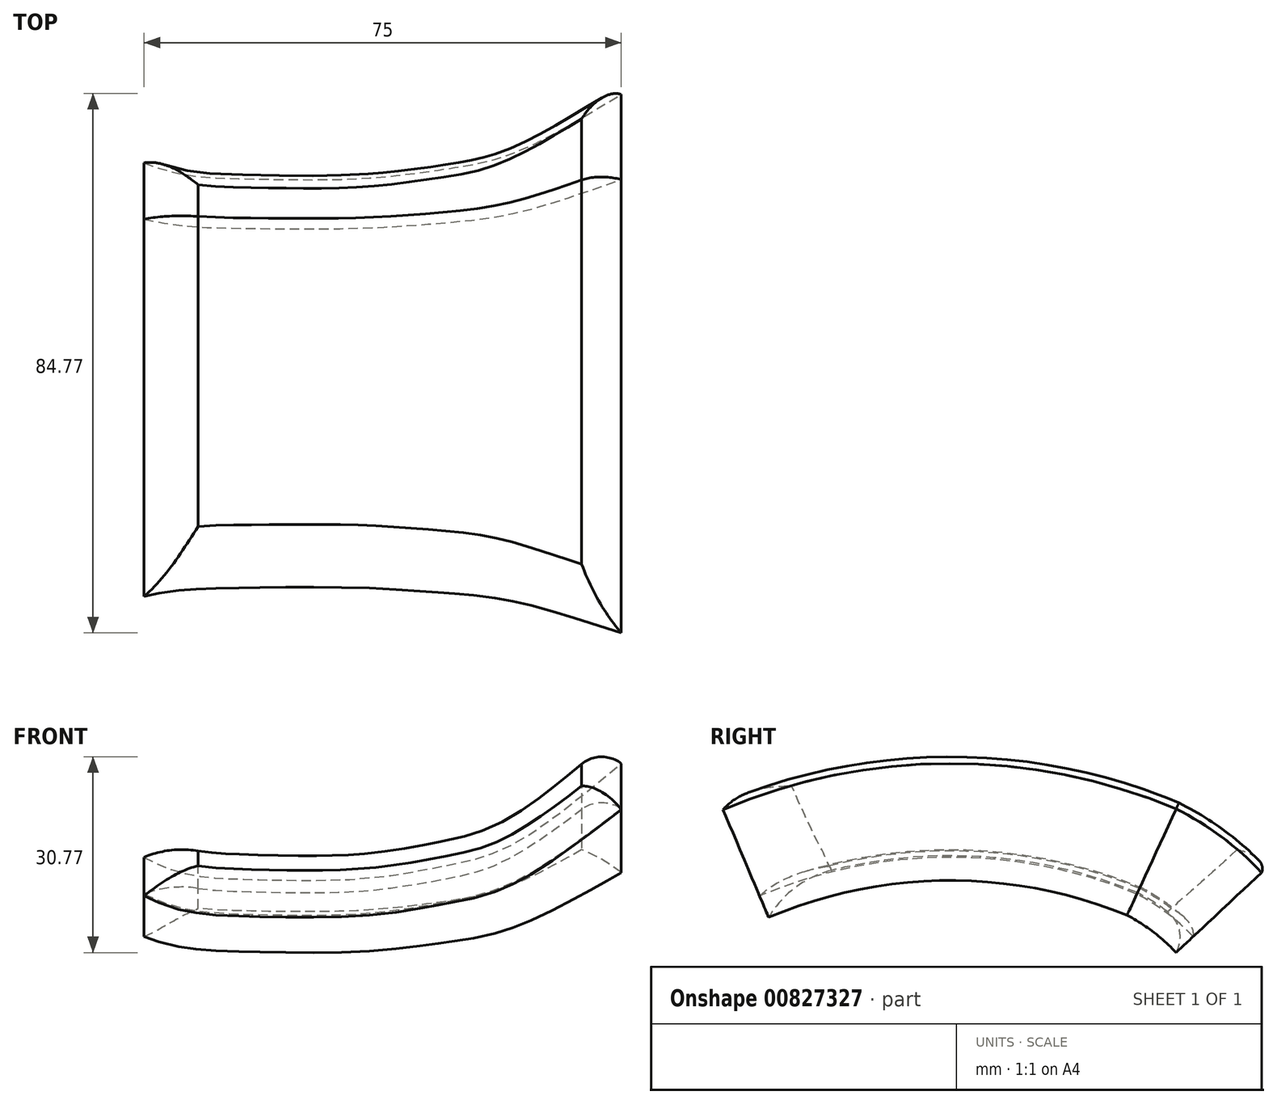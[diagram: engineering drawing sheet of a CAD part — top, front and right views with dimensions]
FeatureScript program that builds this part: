
annotation { "Feature Type Name" : "Feature", "Feature Type Description" : "" }
export const myFeature = defineFeature(function(context is Context, id is Id, definition is map)
    precondition{}
    {
        {
            var Q0;
            Q0=qCreatedBy(makeId("Right.planeOp"),FACE);
            var sketch = newSketch(context, id + "F0", { "sketchPlane" : qUnion([Q0])});
            skArc(sketch, "E0", {"start": v(38.94, 0) * mm, "mid": v(-0.8, 8.06) * mm, "end": v(-40.55, 0) * mm});
            skArc(sketch, "E1", {"start": v(55.58, -12.34) * mm, "mid": v(47.82, -5.42) * mm, "end": v(38.94, 0) * mm});
            skSolve(sketch);
        }
        {
            var Q0;
            Q0=sQuery(id+"F0.wireOp",EDGE,"E1");
            var Q1;
            Q1=sQuery(id+"F0.wireOp",VERTEX,"E1.start");
            cPlane(context, id + "F1", {"entities" : qUnion([Q0, Q1]), "cplaneType" : CPlaneType.CURVE_POINT, "offset" : 25 * mm, "width" : 150 * mm, "height" : 150 * mm});
        }
        {
            var Q0;
            Q0=qCreatedBy(id+"F1.planeOp",FACE);
            var sketch = newSketch(context, id + "F2", { "sketchPlane" : qUnion([Q0])});
            skFitSpline(sketch, "E2", {"points": [v(-32.8, 10.6) * mm, v(-27.57, 8.44) * mm, v(-17.44, 7.52) * mm, v(-0.23, 7.67) * mm, v(12.35, 9.67) * mm, v(21.56, 12.59) * mm, v(32.92, 20.73) * mm, v(37.99, 24.87) * mm], "startDerivative": vector(46.1, -23.5) * mm, "endDerivative": vector(39.35, 32.24) * mm});
            skFitSpline(sketch, "E3.0", {"points": [v(-34.56, 7.14) * mm, v(-34.08, 6.9) * mm, v(-33.06, 6.37) * mm, v(-31.33, 5.58) * mm, v(-29.67, 4.98) * mm, v(-28.2, 4.6) * mm, v(-27.07, 4.36) * mm, v(-25.93, 4.17) * mm, v(-24.37, 3.98) * mm, v(-22.36, 3.82) * mm, v(-20.25, 3.73) * mm, v(-18.5, 3.67) * mm, v(-16.7, 3.62) * mm, v(-14.33, 3.55) * mm, v(-11.34, 3.5) * mm, v(-8.25, 3.48) * mm, v(-5.13, 3.52) * mm, v(-2.03, 3.64) * mm, v(1, 3.87) * mm, v(3.88, 4.2) * mm, v(6.58, 4.61) * mm, v(8.7, 5) * mm, v(10.32, 5.3) * mm, v(11.49, 5.54) * mm, v(12.62, 5.77) * mm, v(13.7, 6) * mm, v(14.8, 6.22) * mm, v(16.28, 6.55) * mm, v(18.18, 7.04) * mm, v(20.17, 7.7) * mm, v(21.8, 8.38) * mm, v(23.05, 8.98) * mm, v(24.32, 9.67) * mm, v(26, 10.66) * mm, v(28.05, 12.04) * mm, v(30.44, 13.79) * mm, v(32.68, 15.54) * mm, v(34.37, 16.9) * mm, v(35.57, 17.89) * mm, v(36.68, 18.78) * mm, v(38.4, 20.2) * mm, v(39.62, 21.2) * mm, v(40.44, 21.87) * mm]});
            skLineSegment(sketch, "E4", {"start": v(37.99, 24.87) * mm, "end": v(40.44, 21.87) * mm});
            skLineSegment(sketch, "E5", {"start": v(-32.8, 10.6) * mm, "end": v(-34.56, 7.14) * mm});
            skSolve(sketch);
        }
        {
            var Q0;
            Q0 = qSketchRegion(id + "F2", true);
            var Q1;
            Q1=sQuery(id+"F0.wireOp",EDGE,"E1");
            var Q2;
            Q2=sQuery(id+"F0.wireOp",EDGE,"E0");
            sweep(context, id + "F3", {"profiles" : qUnion([Q0]), "path" : qUnion([Q1, Q2])});
        }
        {
            var Q0;
            Q0=makeQuery(id+"F3.opSweep","SWEPT_EDGE",EDGE,{"disambiguationData":[OSD([sQuery(id+"F0.wireOp",EDGE,"E0"),sQuery(id+"F2.wireOp",EDGE,"E2"),sQuery(id+"F2.wireOp",EDGE,"E4")])]});
            var Q1;
            Q1=makeQuery(id+"F3.opSweep","SWEPT_EDGE",EDGE,{"disambiguationData":[OSD([sQuery(id+"F0.wireOp",EDGE,"E1"),sQuery(id+"F2.wireOp",EDGE,"E2"),sQuery(id+"F2.wireOp",EDGE,"E4")])]});
            fillet(context, id + "F4", {"entities" : qUnion([Q0, Q1]), "radius" : 5 * mm, "tangentPropagation" : true, "allowEdgeOverflow" : false});
        }
        {
            var Q0;
            {var subQ0=sQuery(id+"F2.wireOp",EDGE,"E4");var subQ1=sQuery(id+"F2.wireOp",EDGE,"E2");Q0=makeQuery(id+"F4.opFillet","BLEND_EDGE",EDGE,{"blendedFrom":[makeQuery(id+"F3.opSweep","SWEPT_EDGE",EDGE,{"disambiguationData":[OSD([sQuery(id+"F0.wireOp",EDGE,"E1"),subQ1,subQ0])]}),makeQuery(id+"F3.opSweep","CAP_FACE",FACE,{"disambiguationData":[OSD([sQuery(id+"F0.wireOp",VERTEX,"E1.start"),subQ1,sQuery(id+"F2.wireOp",EDGE,"E3.0"),sQuery(id+"F2.wireOp",EDGE,"46c48ded-01c2-40fc-bf11-1080ccbc972b"),subQ0])],"isStart":true})],"blendedInto":[makeQuery(id+"F3.opSweep","CAP_FACE",FACE,{"disambiguationData":[OSD([sQuery(id+"F0.wireOp",VERTEX,"E1.start"),subQ1,sQuery(id+"F2.wireOp",EDGE,"E3.0"),sQuery(id+"F2.wireOp",EDGE,"46c48ded-01c2-40fc-bf11-1080ccbc972b"),subQ0])],"isStart":true})]});}
            var Q1;
            Q1=makeQuery(id+"F3.opSweep","CAP_EDGE",EDGE,{"disambiguationData":[OSD([sQuery(id+"F0.wireOp",VERTEX,"E1.start"),sQuery(id+"F2.wireOp",EDGE,"E2")])],"isStart":true});
            fillet(context, id + "F5", {"entities" : qUnion([Q0, Q1]), "radius" : 5 * mm, "tangentPropagation" : true, "allowEdgeOverflow" : false});
        }
        {
            var Q0;
            Q0=makeQuery(id+"F3.opSweep","CAP_EDGE",EDGE,{"disambiguationData":[OSD([sQuery(id+"F0.wireOp",VERTEX,"E0.end"),sQuery(id+"F2.wireOp",EDGE,"E2")])],"isStart":false});
            var Q1;
            {var subQ0=sQuery(id+"F2.wireOp",EDGE,"E4");var subQ1=sQuery(id+"F2.wireOp",EDGE,"E2");Q1=makeQuery(id+"F4.opFillet","BLEND_EDGE",EDGE,{"blendedFrom":[makeQuery(id+"F3.opSweep","SWEPT_EDGE",EDGE,{"disambiguationData":[OSD([sQuery(id+"F0.wireOp",EDGE,"E0"),subQ1,subQ0])]}),makeQuery(id+"F3.opSweep","CAP_FACE",FACE,{"disambiguationData":[OSD([sQuery(id+"F0.wireOp",VERTEX,"E0.end"),subQ1,sQuery(id+"F2.wireOp",EDGE,"E3.0"),sQuery(id+"F2.wireOp",EDGE,"46c48ded-01c2-40fc-bf11-1080ccbc972b"),subQ0])],"isStart":false})],"blendedInto":[makeQuery(id+"F3.opSweep","CAP_FACE",FACE,{"disambiguationData":[OSD([sQuery(id+"F0.wireOp",VERTEX,"E0.end"),subQ1,sQuery(id+"F2.wireOp",EDGE,"E3.0"),sQuery(id+"F2.wireOp",EDGE,"46c48ded-01c2-40fc-bf11-1080ccbc972b"),subQ0])],"isStart":false})]});}
            fillet(context, id + "F6", {"entities" : qUnion([Q0, Q1]), "radius" : 15.93 * mm, "tangentPropagation" : true, "allowEdgeOverflow" : false});
        }
        {
            var Q0;
            Q0=makeQuery(id+"F3.opSweep","SWEPT_EDGE",EDGE,{"disambiguationData":[OSD([sQuery(id+"F0.wireOp",EDGE,"E0"),sQuery(id+"F2.wireOp",EDGE,"E2"),sQuery(id+"F2.wireOp",EDGE,"E5")])]});
            var Q1;
            Q1=makeQuery(id+"F3.opSweep","SWEPT_EDGE",EDGE,{"disambiguationData":[OSD([sQuery(id+"F0.wireOp",EDGE,"E1"),sQuery(id+"F2.wireOp",EDGE,"E2"),sQuery(id+"F2.wireOp",EDGE,"E5")])]});
            var Q2;
            Q2=makeQuery(id+"F5.opFillet","BLEND_EDGE",EDGE,{"blendedFrom":[makeQuery(id+"F3.opSweep","CAP_EDGE",EDGE,{"disambiguationData":[OSD([sQuery(id+"F0.wireOp",VERTEX,"E1.start"),sQuery(id+"F2.wireOp",EDGE,"E2")])],"isStart":true}),makeQuery(id+"F3.opSweep","SWEPT_FACE",FACE,{"disambiguationData":[OSD([sQuery(id+"F0.wireOp",EDGE,"E1"),sQuery(id+"F2.wireOp",EDGE,"E5")])]})],"blendedInto":[makeQuery(id+"F3.opSweep","SWEPT_FACE",FACE,{"disambiguationData":[OSD([sQuery(id+"F0.wireOp",EDGE,"E1"),sQuery(id+"F2.wireOp",EDGE,"E5")])]})]});
            fillet(context, id + "F7", {"entities" : qUnion([Q0, Q1, Q2]), "radius" : 15.22 * mm, "tangentPropagation" : true, "allowEdgeOverflow" : false});
        }
    });
